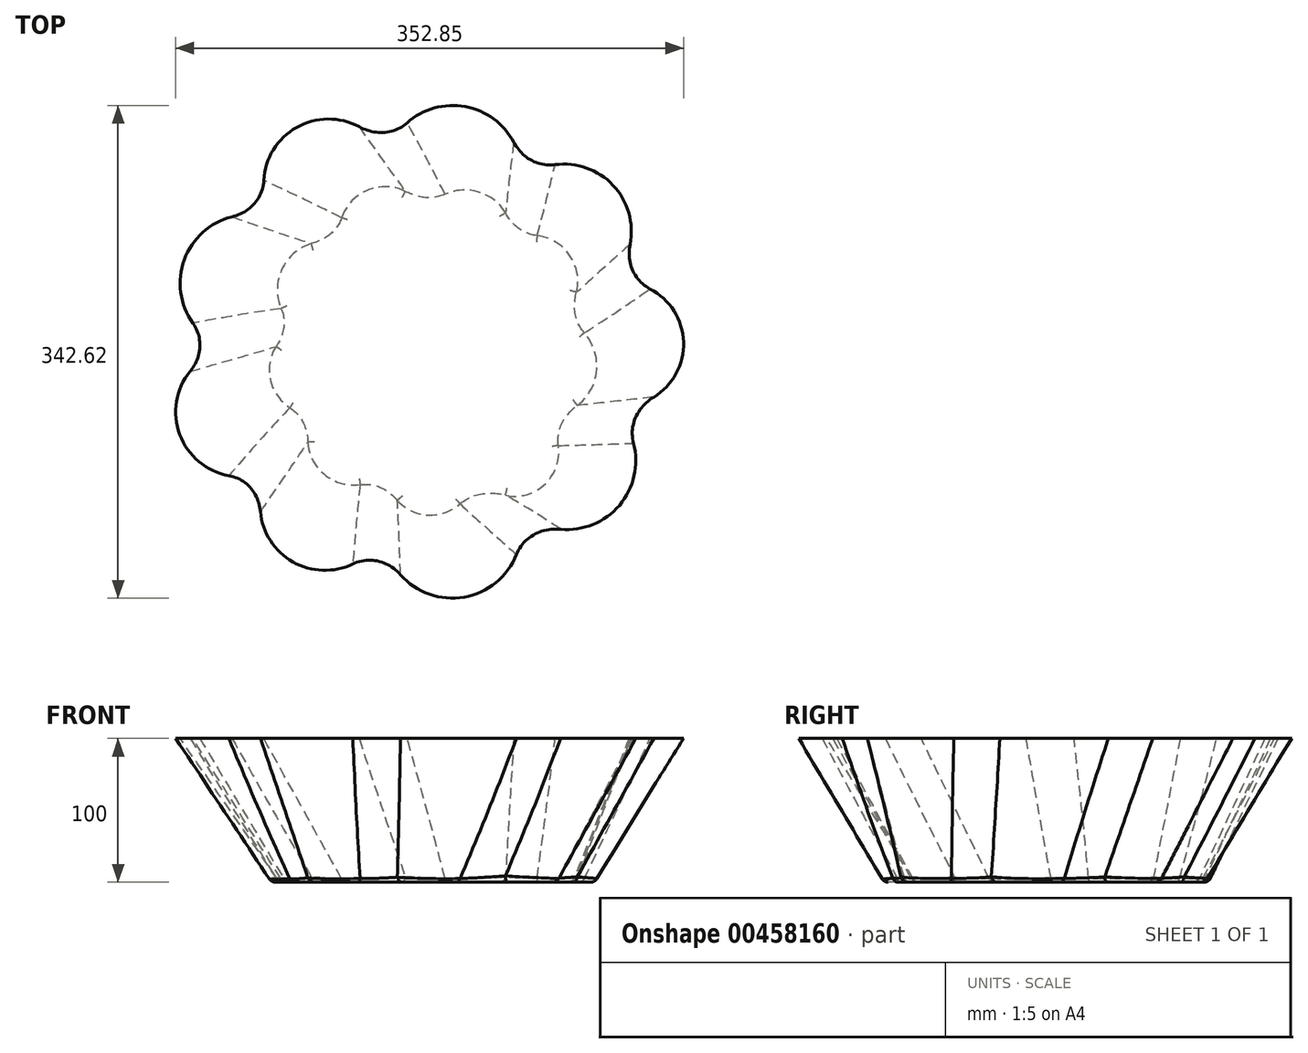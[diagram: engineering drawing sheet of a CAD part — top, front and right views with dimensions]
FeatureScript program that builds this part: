
annotation { "Feature Type Name" : "Feature", "Feature Type Description" : "" }
export const myFeature = defineFeature(function(context is Context, id is Id, definition is map)
    precondition{}
    {
        {
            var Q0;
            Q0=qCreatedBy(makeId("Top.planeOp"),FACE);
            var sketch = newSketch(context, id + "F0", { "sketchPlane" : qUnion([Q0])});
            skPoint(sketch, "E0.0.midPoint", {"position": v(74.24, 44.3) * mm});
            skArc(sketch, "E1", {"start": v(-0.81, 90.93) * mm, "mid": v(-40.05, 106) * mm, "end": v(-58.82, 68.4) * mm});
            skArc(sketch, "E2", {"start": v(-58.82, 68.4) * mm, "mid": v(-99.18, 52.43) * mm, "end": v(-88.1, 10.46) * mm});
            skArc(sketch, "E3", {"start": v(58.1, 70.9) * mm, "mid": v(36.5, 104) * mm, "end": v(-0.81, 90.93) * mm});
            skArc(sketch, "E4", {"start": v(90.37, 17.7) * mm, "mid": v(98.9, 59.25) * mm, "end": v(58.1, 70.9) * mm});
            skArc(sketch, "E5", {"start": v(74.18, -48.49) * mm, "mid": v(115.37, -23.5) * mm, "end": v(90.37, 17.7) * mm});
            skArc(sketch, "E6", {"start": v(-88.1, 10.46) * mm, "mid": v(-107.74, -23.74) * mm, "end": v(-76.52, -47.84) * mm});
            skArc(sketch, "E7", {"start": v(-76.52, -47.84) * mm, "mid": v(-70.24, -89.72) * mm, "end": v(-28, -86.8) * mm});
            skArc(sketch, "E8", {"start": v(-28, -86.8) * mm, "mid": v(2.64, -117.47) * mm, "end": v(31.93, -85.52) * mm});
            skArc(sketch, "E9", {"start": v(31.93, -85.52) * mm, "mid": v(79.77, -97.48) * mm, "end": v(74.18, -48.49) * mm});
            skSolve(sketch);
        }
        {
            var Q0;
            Q0=qCreatedBy(makeId("Top.planeOp"),FACE);
            cPlane(context, id + "F1", {"entities" : qUnion([Q0]), "cplaneType" : CPlaneType.OFFSET, "offset" : 100 * mm, "width" : 150 * mm, "height" : 150 * mm});
        }
        {
            var Q0;
            Q0=qCreatedBy(id+"F1.planeOp",FACE);
            var sketch = newSketch(context, id + "F2", { "sketchPlane" : qUnion([Q0])});
            skPoint(sketch, "E10.0.midPoint", {"position": v(124.48, 0) * mm});
            skPoint(sketch, "E10.cCircle.center.orphan", {"position": v(0, 0) * mm});
            skArc(sketch, "E11", {"start": v(-106, 86.35) * mm, "mid": v(-168.9, 58.6) * mm, "end": v(-138.55, -3.1) * mm});
            skArc(sketch, "E12", {"start": v(-138.55, -3.1) * mm, "mid": v(-172.1, -62.64) * mm, "end": v(-108.13, -86.68) * mm});
            skArc(sketch, "E13", {"start": v(-108.13, -86.68) * mm, "mid": v(-93.68, -151.33) * mm, "end": v(-30.46, -131.52) * mm});
            skArc(sketch, "E14", {"start": v(-30.46, -131.52) * mm, "mid": v(25.71, -176) * mm, "end": v(63.29, -115) * mm});
            skArc(sketch, "E15", {"start": v(63.29, -115) * mm, "mid": v(133.7, -111.95) * mm, "end": v(124.48, -42.07) * mm});
            skArc(sketch, "E16", {"start": v(124.48, -42.07) * mm, "mid": v(178.04, 0) * mm, "end": v(124.48, 42.07) * mm});
            skArc(sketch, "E17", {"start": v(124.48, 42.07) * mm, "mid": v(131.31, 107.87) * mm, "end": v(65.5, 114.7) * mm});
            skArc(sketch, "E18", {"start": v(65.5, 114.7) * mm, "mid": v(26.07, 165.15) * mm, "end": v(-28.24, 131.24) * mm});
            skArc(sketch, "E19", {"start": v(-28.24, 131.24) * mm, "mid": v(-91.2, 150.5) * mm, "end": v(-106, 86.35) * mm});
            skSolve(sketch);
        }
        {
            var Q0;
            Q0=makeQuery(id+"F2.imprint","IMPRINT",FACE,{"disambiguationData":[TD([[makeQuery(id+"F2.imprint","IMPRINT",EDGE,{"derivedFrom":sQuery(id+"F2.wireOp",EDGE,"E11")}),1.0]])]});
            var Q1;
            Q1=makeQuery(id+"F0.imprint","IMPRINT",FACE,{"disambiguationData":[TD([[makeQuery(id+"F0.imprint","IMPRINT",EDGE,{"derivedFrom":sQuery(id+"F0.wireOp",EDGE,"E1")}),1.0]])]});
            loft(context, id + "F3", {"sheetProfilesArray" : [{ "sheetProfileEntities" : qUnion([Q0]) }, { "sheetProfileEntities" : qUnion([Q1]) }]});
        }
        {
            var Q0;
            Q0=makeQuery(id+"F3.opLoft","SWEPT_EDGE",EDGE,{"disambiguationData":[OSD([sQuery(id+"F0.wireOp",EDGE,"E7"),sQuery(id+"F0.wireOp",EDGE,"E8"),sQuery(id+"F2.wireOp",EDGE,"E13"),sQuery(id+"F2.wireOp",EDGE,"E14")])]});
            var Q1;
            Q1=makeQuery(id+"F3.opLoft","SWEPT_EDGE",EDGE,{"disambiguationData":[OSD([sQuery(id+"F0.wireOp",EDGE,"E6"),sQuery(id+"F0.wireOp",EDGE,"E7"),sQuery(id+"F2.wireOp",EDGE,"E12"),sQuery(id+"F2.wireOp",EDGE,"E13")])]});
            var Q2;
            Q2=makeQuery(id+"F3.opLoft","SWEPT_EDGE",EDGE,{"disambiguationData":[OSD([sQuery(id+"F0.wireOp",EDGE,"E2"),sQuery(id+"F0.wireOp",EDGE,"E6"),sQuery(id+"F2.wireOp",EDGE,"E11"),sQuery(id+"F2.wireOp",EDGE,"E12")])]});
            var Q3;
            Q3=makeQuery(id+"F3.opLoft","SWEPT_EDGE",EDGE,{"disambiguationData":[OSD([sQuery(id+"F0.wireOp",EDGE,"E1"),sQuery(id+"F0.wireOp",EDGE,"E2"),sQuery(id+"F2.wireOp",EDGE,"E11"),sQuery(id+"F2.wireOp",EDGE,"E19")])]});
            var Q4;
            Q4=makeQuery(id+"F3.opLoft","SWEPT_EDGE",EDGE,{"disambiguationData":[OSD([sQuery(id+"F0.wireOp",EDGE,"E1"),sQuery(id+"F0.wireOp",EDGE,"E3"),sQuery(id+"F2.wireOp",EDGE,"E18"),sQuery(id+"F2.wireOp",EDGE,"E19")])]});
            var Q5;
            Q5=makeQuery(id+"F3.opLoft","SWEPT_EDGE",EDGE,{"disambiguationData":[OSD([sQuery(id+"F0.wireOp",EDGE,"E3"),sQuery(id+"F0.wireOp",EDGE,"E4"),sQuery(id+"F2.wireOp",EDGE,"E17"),sQuery(id+"F2.wireOp",EDGE,"E18")])]});
            var Q6;
            Q6=makeQuery(id+"F3.opLoft","SWEPT_EDGE",EDGE,{"disambiguationData":[OSD([sQuery(id+"F0.wireOp",EDGE,"E5"),sQuery(id+"F0.wireOp",EDGE,"E9"),sQuery(id+"F2.wireOp",EDGE,"E15"),sQuery(id+"F2.wireOp",EDGE,"E16")])]});
            var Q7;
            Q7=makeQuery(id+"F3.opLoft","SWEPT_EDGE",EDGE,{"disambiguationData":[OSD([sQuery(id+"F0.wireOp",EDGE,"E4"),sQuery(id+"F0.wireOp",EDGE,"E5"),sQuery(id+"F2.wireOp",EDGE,"E16"),sQuery(id+"F2.wireOp",EDGE,"E17")])]});
            var Q8;
            Q8=makeQuery(id+"F3.opLoft","SWEPT_EDGE",EDGE,{"disambiguationData":[OSD([sQuery(id+"F0.wireOp",EDGE,"E8"),sQuery(id+"F0.wireOp",EDGE,"E9"),sQuery(id+"F2.wireOp",EDGE,"E14"),sQuery(id+"F2.wireOp",EDGE,"E15")])]});
            fillet(context, id + "F4", {"entities" : qUnion([Q0, Q1, Q2, Q3, Q4, Q5, Q6, Q7, Q8]), "radius" : 30 * mm, "tangentPropagation" : true, "allowEdgeOverflow" : false});
        }
        {
            var Q0;
            Q0=makeQuery(id+"F3.opLoft","CAP_FACE",FACE,{"disambiguationData":[OSD([makeQuery(id+"F0.imprint","IMPRINT",FACE,{"disambiguationData":[TD([[makeQuery(id+"F0.imprint","IMPRINT",EDGE,{"derivedFrom":sQuery(id+"F0.wireOp",EDGE,"E1")}),1.0]])]})])],"isStart":true});
            var Q1;
            {var subQ0=sQuery(id+"F0.wireOp",EDGE,"E2");var subQ1=sQuery(id+"F0.wireOp",EDGE,"E6");Q1=makeQuery(id+"F4.opFillet","BLEND_EDGE",EDGE,{"blendedFrom":[makeQuery(id+"F3.opLoft","SWEPT_EDGE",EDGE,{"disambiguationData":[OSD([subQ0,subQ1,sQuery(id+"F2.wireOp",EDGE,"E11"),sQuery(id+"F2.wireOp",EDGE,"E12")])]}),makeQuery(id+"F3.opLoft","CAP_FACE",FACE,{"disambiguationData":[OSD([makeQuery(id+"F0.imprint","IMPRINT",FACE,{"disambiguationData":[TD([[makeQuery(id+"F0.imprint","IMPRINT",EDGE,{"derivedFrom":sQuery(id+"F0.wireOp",EDGE,"E1")}),1.0]])]})])],"isStart":true})],"blendedInto":[makeQuery(id+"F3.opLoft","CAP_FACE",FACE,{"disambiguationData":[OSD([makeQuery(id+"F0.imprint","IMPRINT",FACE,{"disambiguationData":[TD([[makeQuery(id+"F0.imprint","IMPRINT",EDGE,{"derivedFrom":sQuery(id+"F0.wireOp",EDGE,"E1")}),1.0]])]})])],"isStart":true})]});}
            fillet(context, id + "F5", {"entities" : qUnion([Q0, Q1]), "radius" : 5 * mm, "tangentPropagation" : true, "allowEdgeOverflow" : false});
        }
    });
